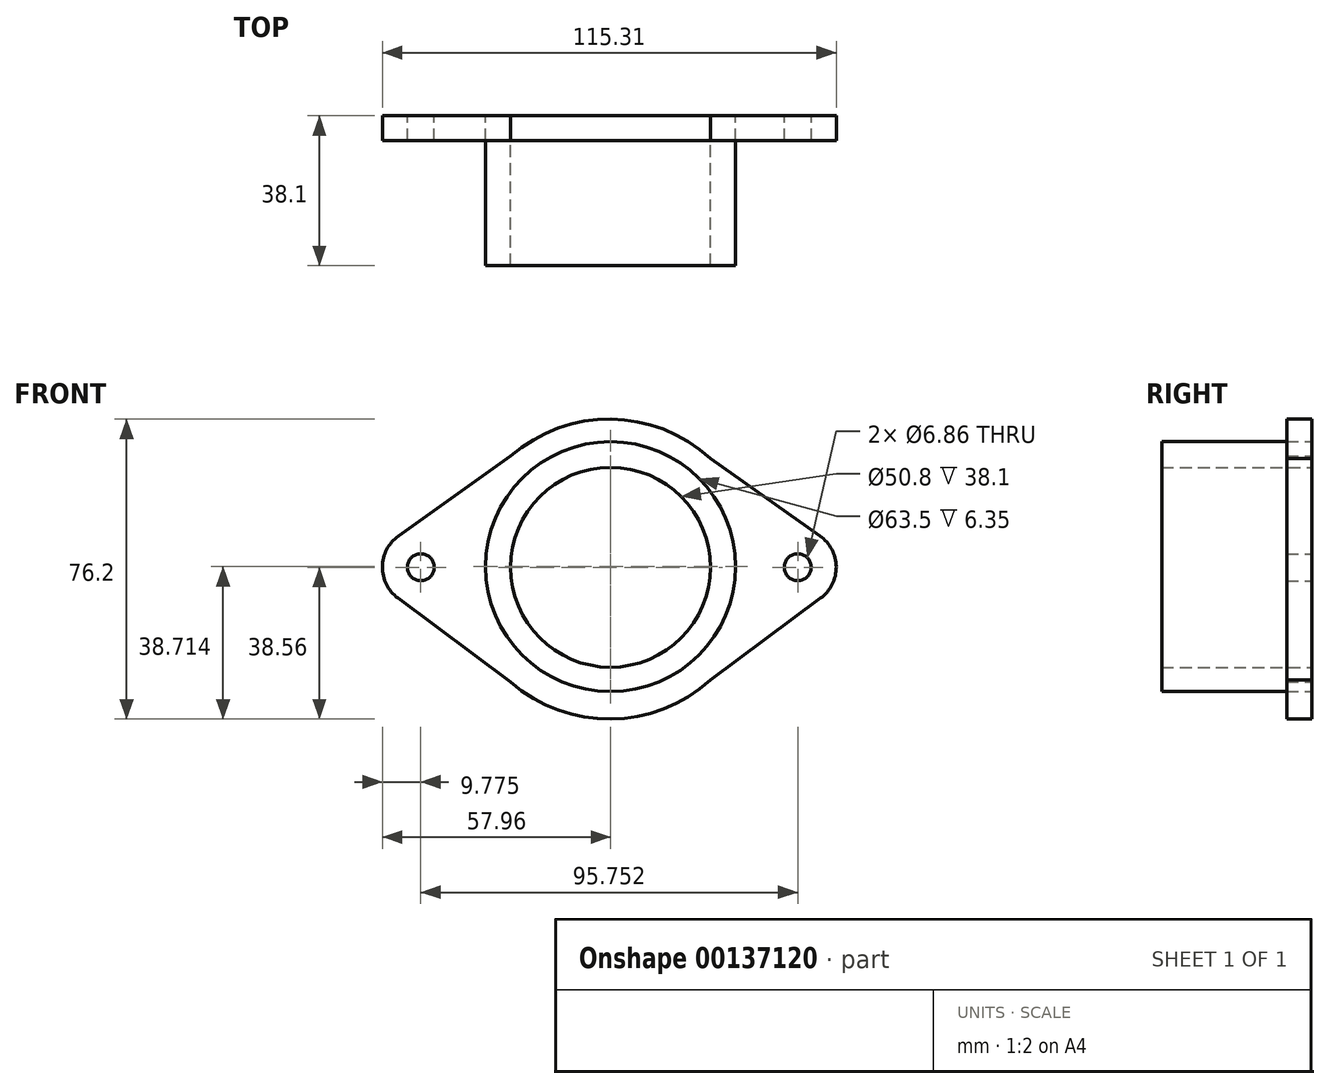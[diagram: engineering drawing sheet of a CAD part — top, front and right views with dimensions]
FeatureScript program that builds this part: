
annotation { "Feature Type Name" : "Feature", "Feature Type Description" : "" }
export const myFeature = defineFeature(function(context is Context, id is Id, definition is map)
    precondition{}
    {
        {
            var Q0;
            Q0=qCreatedBy(makeId("Front.planeOp"),FACE);
            var sketch = newSketch(context, id + "F0", { "sketchPlane" : qUnion([Q0])});
            skCircle(sketch, "E0", {"center": v(0, 0) * mm, "radius": 25.4 * mm});
            skCircle(sketch, "E1", {"center": v(0, 0.15) * mm, "radius": 31.75 * mm});
            skArc(sketch, "E2", {"start": v(25.4, 27.66) * mm, "mid": v(0.1, 37.63) * mm, "end": v(-25.4, 28.2) * mm});
            skArc(sketch, "E3", {"start": v(53.39, -7.86) * mm, "mid": v(57.35, 0.1) * mm, "end": v(53.21, 7.98) * mm});
            skCircle(sketch, "E4", {"center": v(47.57, 0) * mm, "radius": 3.43 * mm});
            skArc(sketch, "E5", {"start": v(-53.85, 7.97) * mm, "mid": v(-57.96, 0.1) * mm, "end": v(-54.02, -7.85) * mm});
            skCircle(sketch, "E6", {"center": v(-48.18, 0) * mm, "radius": 3.43 * mm});
            skLineSegment(sketch, "E7", {"start": v(-25.4, -29.13) * mm, "end": v(-54.02, -7.85) * mm});
            skLineSegment(sketch, "E8", {"start": v(-25.4, 28.2) * mm, "end": v(-53.85, 7.97) * mm});
            skLineSegment(sketch, "E9", {"start": v(25.4, 27.66) * mm, "end": v(53.21, 7.98) * mm});
            skLineSegment(sketch, "E10", {"start": v(25.4, -28.58) * mm, "end": v(53.39, -7.86) * mm});
            skArc(sketch, "E11.trimOffspring", {"start": v(-25.4, -29.13) * mm, "mid": v(0.1, -38.56) * mm, "end": v(25.4, -28.58) * mm});
            skSolve(sketch);
        }
        {
            var Q0;
            Q0=makeQuery(id+"F0.imprint","IMPRINT",FACE,{"disambiguationData":[TD([[makeQuery(id+"F0.imprint","IMPRINT",EDGE,{"derivedFrom":sQuery(id+"F0.wireOp",EDGE,"E1")}),-1.0]])]});
            extrude(context, id + "F1", {"entities" : qUnion([Q0]), "depth" : 6.35 * mm});
        }
        {
            var Q0;
            Q0=makeQuery(id+"F0.imprint","IMPRINT",FACE,{"disambiguationData":[TD([[makeQuery(id+"F0.imprint","IMPRINT",EDGE,{"derivedFrom":sQuery(id+"F0.wireOp",EDGE,"E0")}),-1.0]])]});
            extrude(context, id + "F2", {"entities" : qUnion([Q0]), "depth" : 38.1 * mm});
        }
    });
